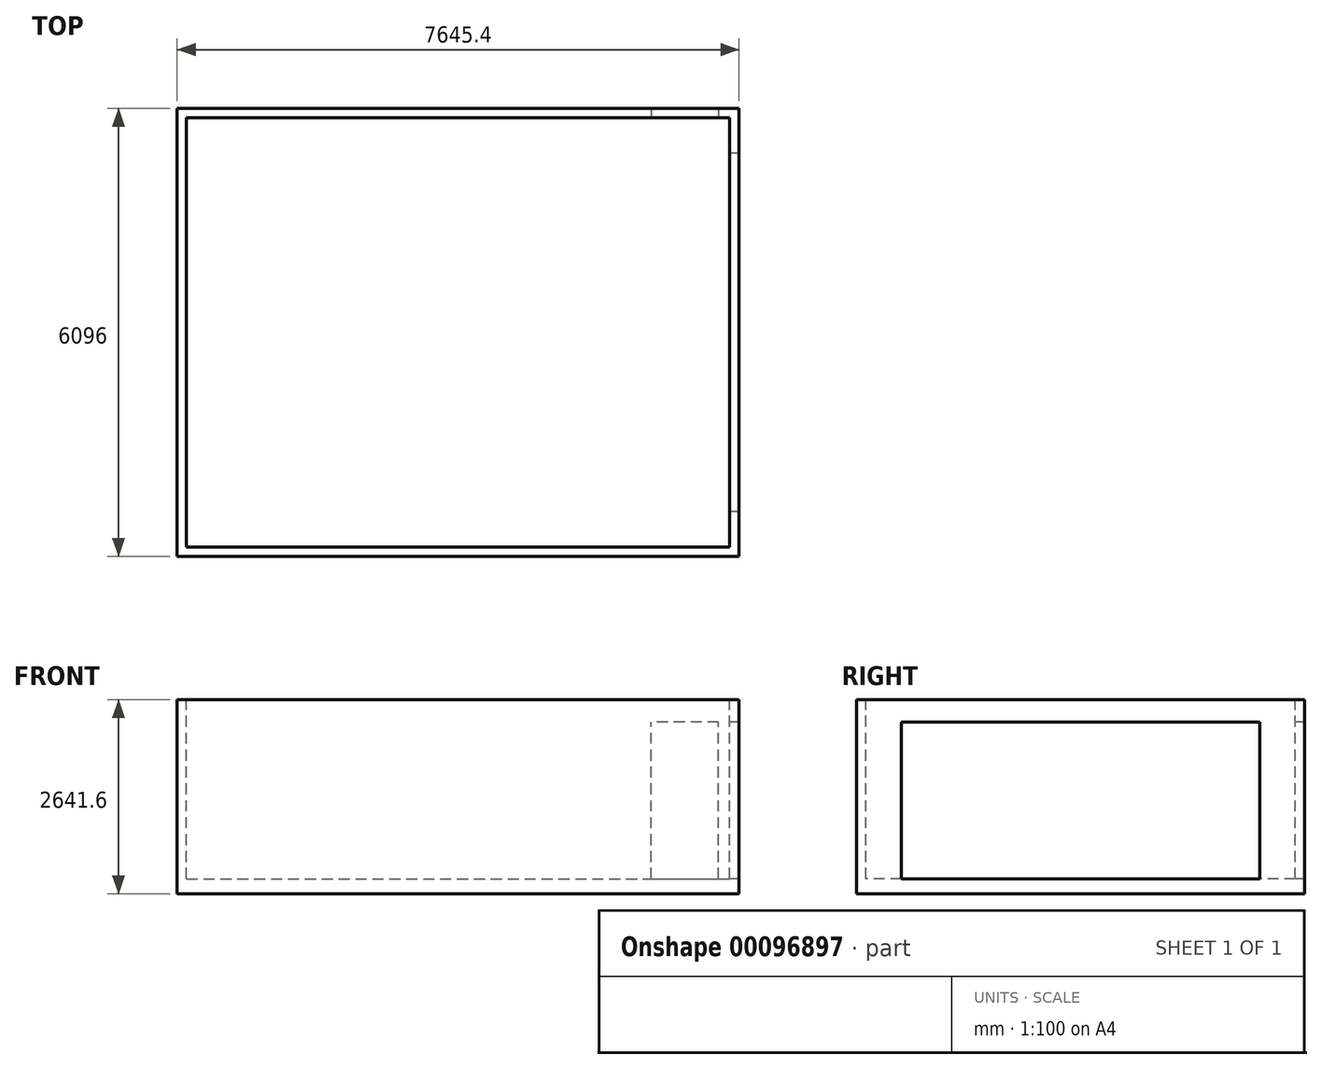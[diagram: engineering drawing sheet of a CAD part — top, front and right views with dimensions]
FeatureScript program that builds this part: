
annotation { "Feature Type Name" : "Feature", "Feature Type Description" : "" }
export const myFeature = defineFeature(function(context is Context, id is Id, definition is map)
    precondition{}
    {
        {
            var Q0;
            Q0=qCreatedBy(makeId("Top.planeOp"),FACE);
            var sketch = newSketch(context, id + "F0", { "sketchPlane" : qUnion([Q0])});
            skLineSegment(sketch, "E0.bottom", {"start": v(0, 0) * mm, "end": v(7645.4, 0) * mm});
            skLineSegment(sketch, "E0.top", {"start": v(0, 6096) * mm, "end": v(7645.4, 6096) * mm});
            skLineSegment(sketch, "E0.left", {"start": v(0, 0) * mm, "end": v(0, 6096) * mm});
            skLineSegment(sketch, "E0.right", {"start": v(7645.4, 0) * mm, "end": v(7645.4, 6096) * mm});
            skSolve(sketch);
        }
        {
            var Q0;
            Q0 = qSketchRegion(id + "F0", true);
            extrude(context, id + "F1", {"entities" : qUnion([Q0]), "depth" : 2641.6 * mm});
        }
        {
            var Q0;
            Q0=makeQuery(id+"F1.opExtrude","CAP_FACE",FACE,{"disambiguationData":[OSD([sQuery(id+"F0.wireOp",EDGE,"E0.bottom"),sQuery(id+"F0.wireOp",EDGE,"E0.top"),sQuery(id+"F0.wireOp",EDGE,"E0.left"),sQuery(id+"F0.wireOp",EDGE,"E0.right")])],"isStart":false});
            var sketch = newSketch(context, id + "F2", { "sketchPlane" : qUnion([Q0])});
            skLineSegment(sketch, "E1.bottom", {"start": v(127, 5969) * mm, "end": v(7518.4, 5969) * mm});
            skLineSegment(sketch, "E1.top", {"start": v(127, 127) * mm, "end": v(7518.4, 127) * mm});
            skLineSegment(sketch, "E1.left", {"start": v(127, 5969) * mm, "end": v(127, 127) * mm});
            skLineSegment(sketch, "E1.right", {"start": v(7518.4, 5969) * mm, "end": v(7518.4, 127) * mm});
            skSolve(sketch);
        }
        {
            var Q0;
            Q0 = qSketchRegion(id + "F2", true);
            extrude(context, id + "F3", {"entities" : qUnion([Q0]), "operationType" : NewBodyOperationType.REMOVE, "oppositeDirection" : true, "depth" : 2438.4 * mm});
        }
        {
            var Q0;
            Q0=makeQuery(id+"F3.boolean.opBoolean","COPY",FACE,{"derivedFrom":makeQuery(id+"F3.opExtrude","SWEPT_FACE",FACE,{"disambiguationData":[OSD([sQuery(id+"F2.wireOp",EDGE,"E1.right")])]})});
            var sketch = newSketch(context, id + "F4", { "sketchPlane" : qUnion([Q0])});
            skLineSegment(sketch, "E2.bottom", {"start": v(-5486.4, 203.2) * mm, "end": v(-609.6, 203.2) * mm});
            skLineSegment(sketch, "E2.top", {"start": v(-5486.4, 2336.8) * mm, "end": v(-609.6, 2336.8) * mm});
            skLineSegment(sketch, "E2.left", {"start": v(-5486.4, 203.2) * mm, "end": v(-5486.4, 2336.8) * mm});
            skLineSegment(sketch, "E2.right", {"start": v(-609.6, 203.2) * mm, "end": v(-609.6, 2336.8) * mm});
            skSolve(sketch);
        }
        {
            var Q0;
            Q0 = qSketchRegion(id + "F4", true);
            extrude(context, id + "F5", {"entities" : qUnion([Q0]), "operationType" : NewBodyOperationType.REMOVE, "endBound" : BoundingType.UP_TO_NEXT, "oppositeDirection" : true, "depth" : 25.4 * mm});
        }
        {
            var Q0;
            Q0=makeQuery(id+"F3.boolean.opBoolean","COPY",FACE,{"derivedFrom":makeQuery(id+"F3.opExtrude","SWEPT_FACE",FACE,{"disambiguationData":[OSD([sQuery(id+"F2.wireOp",EDGE,"E1.bottom")])]})});
            var sketch = newSketch(context, id + "F6", { "sketchPlane" : qUnion([Q0])});
            skLineSegment(sketch, "E3.bottom", {"start": v(7366, 203.2) * mm, "end": v(6451.6, 203.2) * mm});
            skLineSegment(sketch, "E3.top", {"start": v(7366, 2336.8) * mm, "end": v(6451.6, 2336.8) * mm});
            skLineSegment(sketch, "E3.left", {"start": v(7366, 203.2) * mm, "end": v(7366, 2336.8) * mm});
            skLineSegment(sketch, "E3.right", {"start": v(6451.6, 203.2) * mm, "end": v(6451.6, 2336.8) * mm});
            skSolve(sketch);
        }
        {
            var Q0;
            Q0 = qSketchRegion(id + "F6", true);
            extrude(context, id + "F7", {"entities" : qUnion([Q0]), "operationType" : NewBodyOperationType.REMOVE, "endBound" : BoundingType.UP_TO_NEXT, "oppositeDirection" : true, "depth" : 25.4 * mm});
        }
    });
